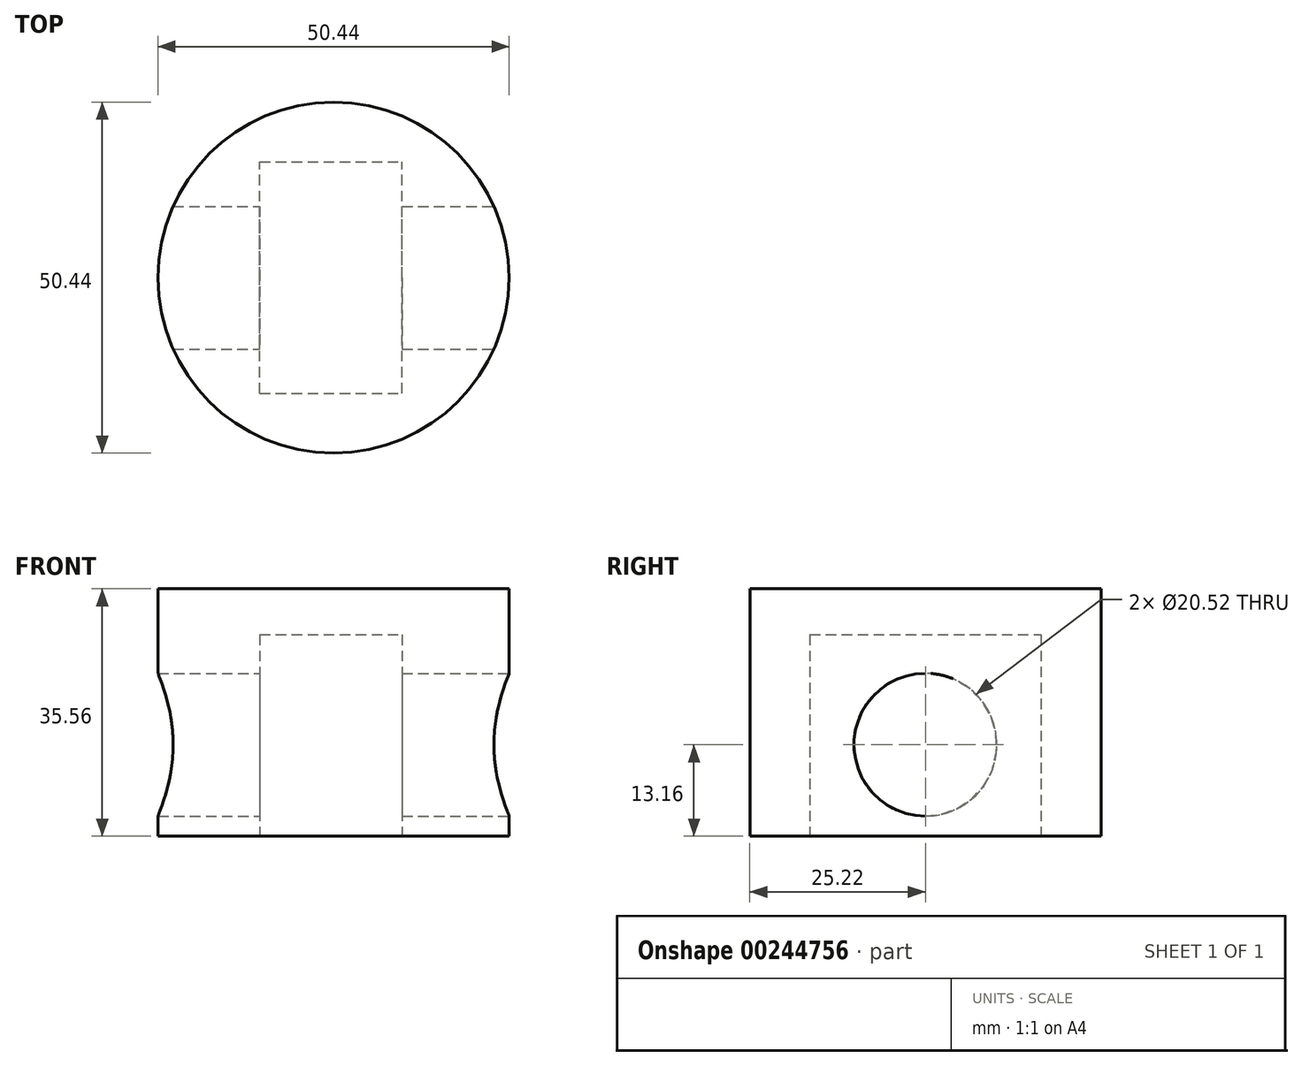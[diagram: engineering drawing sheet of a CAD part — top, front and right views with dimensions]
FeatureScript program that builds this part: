
annotation { "Feature Type Name" : "Feature", "Feature Type Description" : "" }
export const myFeature = defineFeature(function(context is Context, id is Id, definition is map)
    precondition{}
    {
        {
            var Q0;
            Q0=qCreatedBy(makeId("Top.planeOp"),FACE);
            var sketch = newSketch(context, id + "F0", { "sketchPlane" : qUnion([Q0])});
            skCircle(sketch, "E0", {"center": v(0, 0) * mm, "radius": 25.22 * mm});
            skSolve(sketch);
        }
        {
            var Q0;
            Q0 = qSketchRegion(id + "F0", true);
            extrude(context, id + "F1", {"entities" : qUnion([Q0]), "depth" : 35.56 * mm});
        }
        {
            var Q0;
            Q0=qCreatedBy(makeId("Top.planeOp"),FACE);
            var sketch = newSketch(context, id + "F2", { "sketchPlane" : qUnion([Q0])});
            skLineSegment(sketch, "E1.bottom", {"start": v(-10.6, -16.62) * mm, "end": v(9.84, -16.62) * mm});
            skLineSegment(sketch, "E1.top", {"start": v(-10.6, 16.62) * mm, "end": v(9.84, 16.62) * mm});
            skLineSegment(sketch, "E1.left", {"start": v(-10.6, -16.62) * mm, "end": v(-10.6, 16.62) * mm});
            skLineSegment(sketch, "E1.right", {"start": v(9.84, -16.62) * mm, "end": v(9.84, 16.62) * mm});
            skSolve(sketch);
        }
        {
            var Q0;
            Q0 = qSketchRegion(id + "F2", true);
            extrude(context, id + "F3", {"entities" : qUnion([Q0]), "operationType" : NewBodyOperationType.REMOVE, "depth" : 28.96 * mm});
        }
        {
            var Q0;
            Q0=qCreatedBy(makeId("Right.planeOp"),FACE);
            cPlane(context, id + "F4", {"entities" : qUnion([Q0]), "cplaneType" : CPlaneType.OFFSET, "offset" : 30.23 * mm, "width" : 152.4 * mm, "height" : 152.4 * mm});
        }
        {
            var Q0;
            Q0=qCreatedBy(id+"F4.planeOp",FACE);
            var sketch = newSketch(context, id + "F5", { "sketchPlane" : qUnion([Q0])});
            skCircle(sketch, "E2", {"center": v(0, 13.16) * mm, "radius": 10.26 * mm});
            skSolve(sketch);
        }
        {
            var Q0;
            Q0=makeQuery(id+"F5.imprint","IMPRINT",FACE,{"disambiguationData":[TD([[makeQuery(id+"F5.imprint","IMPRINT",EDGE,{"derivedFrom":sQuery(id+"F5.wireOp",EDGE,"E2")}),1.0]])]});
            extrude(context, id + "F6", {"entities" : qUnion([Q0]), "operationType" : NewBodyOperationType.REMOVE, "oppositeDirection" : true, "depth" : 65.53 * mm});
        }
    });
